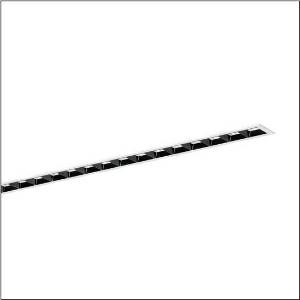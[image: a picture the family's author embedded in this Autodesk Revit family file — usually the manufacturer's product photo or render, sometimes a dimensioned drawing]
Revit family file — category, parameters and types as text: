
# Revit family: silica_21_51mx14da34wb
name_source: partatom
category: Lighting Fixtures
units: mm (PartAtom-declared; Revit-internal decimal feet)

## family parameters
Cut with Voids When Loaded = No
Host = Face
Light Source = No
Part Type = Normal
Room Calculation Point = No
Round Connector Dimension = Use Diameter
Shared = No

## types (1)
- --- (1 x LED, 4320 lm, 32.1 W, 3000K)
    Apparent Load = 32 VA
    CIE Flux Codes = 74 94 99 100 100
    Color Rendering = 80
    Color Temperature = 3000K
    Default Elevation = 1800 mm
    Description = Silica 21, office luminaire, primary light control with darklight reflector, of PMMA, black, light emission: direct distribution, primary light characteristic: asymmetric, installation type: recessed, LED, rated luminous flux: 4.320lm, luminous efficacy: 135lm/W, light colour: 830, colour temperature: 3000K, control gear: DALI 2, with terminal, 3+2-pole, max. 2.5mm², mains connection: 220..240V, AC, 50/60Hz, rated input power: 32.1W, luminaire housing, of aluminium, traffic white (RAL 9016), length: 1.228mm, width: 79mm, height: 53mm, protection rating (complete): IP20, insulation class (complete): insulation class I (protective earthing), certification: CE, ENEC, VDE, permissible operating ambient temperature: 0..+35°C, standard: EN 50419, packaging unit: 1 piece
    Height = 0 mm  [stored 0 ft]
    Lamp = 1 x LED
    Lamp Light Flux = 4320 lm
    Lamp Power = 32.1 W
    Lamp count = 1
    Length = 1227 mm
    Luminous efficacy = 135 lm/W
    Manufacturer = Siteco
    ModVariant = No
    Model = 51MX14DA34WB
    Mounting Place = Ceiling
    Mounting Type = Recessed
    Number of Poles = 1
    OnlyDefault = Yes
    Power Factor = 1
    Product Name = Silica 21
    Product group = office luminaire | ceiling recessed
    ProductGroupID = 400
    Protection Class = Protection class I
    Protection Degree = IP 20
    RLX_Detail_Level = 1
    RLX_Emergency_Light_Flux = 0 lm
    RLX_Emergency_Type = 0
    RLX_Emergency_Type_DB = No
    RlxData = <blob elided: 39609 chars, md5=039cde5c>
    Socket = socket
    Standby Power = 0 W
    System Light Flux = 4320 lm
    System Power = 32 W
    Type Comments = factory setting: luminous flux: 100 % | dim-lin: 254 | 448 mA
    Type Image = l_1335880.jpg
    URL = http://relux.com
    VarID = @adj_122655
    Voltage = 0 V
    Weight = 0.00 kg
    Width = 79 mm

note: [stored X ft] marks values corroborated as IEEE doubles in the binary element streams (Revit-internal decimal feet)

## geometry (parser evidence)
native form markers: Blend x4, Sweep x10
no freeform markers — native parametric forms only
